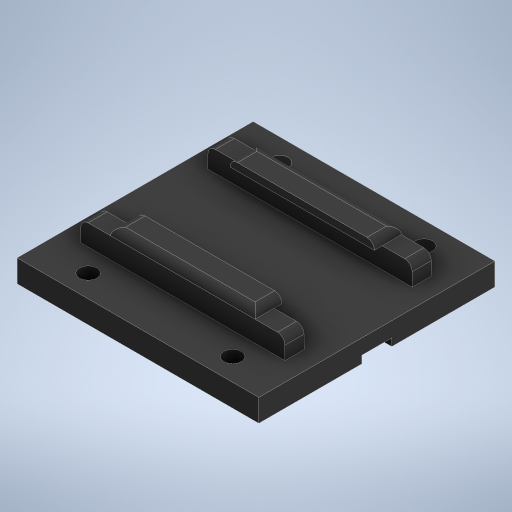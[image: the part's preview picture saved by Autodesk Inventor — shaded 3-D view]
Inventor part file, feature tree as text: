
AUTODESK INVENTOR PART (.ipt)
format: ipt  version: 2024 (Build 280153000, 153)  size: 431,616 bytes
history: native  units: in
note: dims shown in document units (in); Inventor stores cm internally (conversion verified against a paired STEP export)
features: projected_geometry x8, extrude x6, sketch x6, fillet x3
ambient origin geometry x8: Origin, YZ Plane, XZ Plane, XY Plane, X Axis, Y Axis, Z Axis, Center Point
bodies: Solid1 (feature_tree)
feature tree (23):
  extrude  "Extrusion1"  Depth=0.673in
  extrude  "Extrusion2"  Depth=0.2in
  extrude  "Extrusion4"  Depth=0.1in TaperAngle=0.0deg
  fillet  "Fillet1"  Radius=0.05in
  fillet  "Fillet3"  Radius=0.14in
  extrude  "Extrusion7"  Depth=0.1in
  fillet  "Fillet4"  Radius=0.05in
  extrude  "Extrusion8"  Depth=0.4in
  extrude  "Extrusion9"  Depth=0.1in
  sketch  "Sketch12"  dims[d35=0.4in d36=0.1in d37=0.1in d38=0.0275in d39=0.0275in d40=0.05in d41=0.2in d42=0.2in d43=0.18in d44=0.05in d45=0.0in d46=0.05in d47=0.125in d48=0.125in d49=0.125in d50=0.125in d51=0.15in d52=0.0in d53=0.15in d54=0.0in]
  sketch  "Sketch1"  dims[d0=1.26in d1=0.673in]
  sketch  "Sketch4"  dims[d2=0.4in d3=0.2in]
  projected_geometry  "Projected Loop1"
  projected_geometry  "Projected Loop9"
  sketch  "Sketch8"  dims[d4=0.1181in d5=0.1in d6=0.0in d10=0.05in d12=0.14in d13=0.0in]
  sketch  "Sketch9"  dims[d16=0.1in d17=0.1in d18=0.05in d19=0.0in]
  projected_geometry  "Projected Loop10"
  projected_geometry  "Projected Loop11"
  projected_geometry  "Projected Loop12"
  sketch  "Sketch11"  dims[d22=0.25in d34=0.4in]
  projected_geometry  "Projected Loop13"
  projected_geometry  "Projected Loop14"
  projected_geometry  "Projected Loop15"
